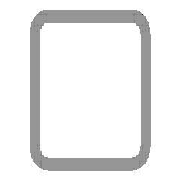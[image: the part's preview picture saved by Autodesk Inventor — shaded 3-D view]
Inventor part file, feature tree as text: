
AUTODESK INVENTOR PART (.ipt)
format: ipt  version: 2025.1 (Build 291241020, 241B)  size: 142,336 bytes
history: native  units: mm (DEFAULTED — no unit token found)
features: other x4, sketch x1, plane x1
ambient origin geometry x8: Origin, YZ Plane, XZ Plane, XY Plane, X Axis, Y Axis, Z Axis, Center Point
bodies: Solid1 (feature_tree), Body (feature_tree)
feature tree (6):
  parser-record x1  (decoder bookkeeping rows leaked as tree rows — omitted from the tree; the rows remain in map.json)
  other  "Driven Length"
  other  "Start Plane"
  other  "End Plane"
  sketch  "Sketch3"  dims[d3=1350.0mm d4=0.0mm d7=4.0mm d9=40.0mm d11=40.0mm d12=2.0mm d13=50.0mm d14=1400.0mm d15=20.0mm d16=20.0mm d17=90.0deg d18=1350.0mm]
  plane  "Work Plane3"
